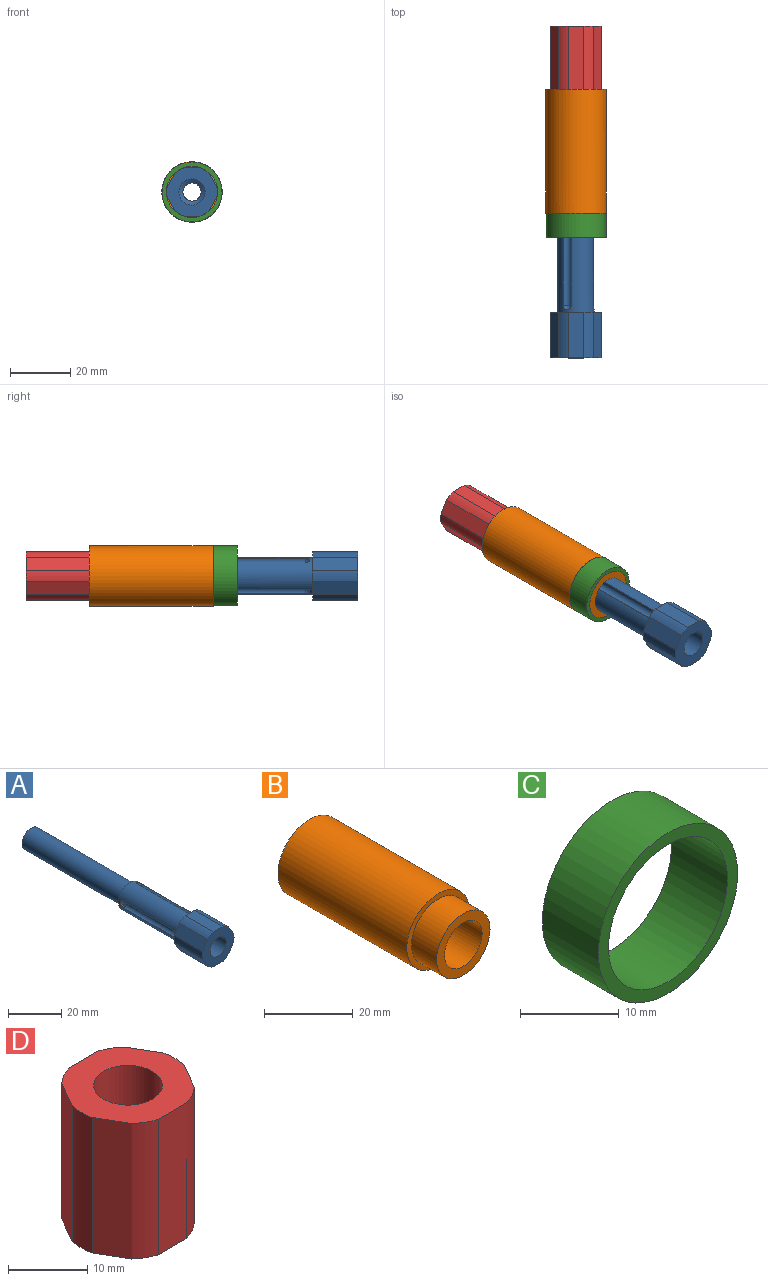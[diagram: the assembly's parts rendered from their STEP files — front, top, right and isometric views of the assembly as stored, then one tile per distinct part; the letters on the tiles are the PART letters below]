
ASSEMBLY  parts=4 mates=6
PART A: 30 faces, bbox 16.8x99.5x16 mm
  f0: sphere r=1.53mm, area 6.9mm2, adj f11,f29
  f1: sphere r=1.53mm, area 6.9mm2, adj f11,f29
  f2: sphere r=1.53mm, area 6.9mm2, adj f11,f28
  f3: sphere r=1.53mm, area 6.9mm2, adj f11,f28
  f4: sphere r=1.53mm, area 6.9mm2, adj f11,f27
  f5: sphere r=1.53mm, area 6.9mm2, adj f11,f27
  f6: cylinder r=8.4mm len=15mm, axis (0,1,0), area 53.9mm2, adj f12,f13,f16,f17
  f7: cylinder r=3mm len=84.69mm, axis (0,1,0), area 1596.3mm2, adj f8,f20
  f8: cone r=4.35mm half-angle=59deg, axis (0,-1,0), area 36.4mm2, adj f7,f9
  f9: cylinder r=4.35mm len=14mm, axis (0,1,0), area 382.6mm2, adj f8,f12
  f10: cylinder r=4.75mm len=52.5mm, axis (0,1,0), area 1566.9mm2, adj f20,f21
  f11: cylinder r=6mm len=32mm, axis (0,1,0), area 944.7mm2, adj f0,f1,f2,f3,f4,f5,f13,f21
  f12: plane 16.8x16mm, normal (0,-1,0), area 154mm2, adj f6,f9,f14,f15,f16,f17,f18,f19
  f13: plane 16.8x16mm, normal (0,1,0), area 100.3mm2, adj f6,f11,f14,f15,f16,f17,f18,f19
  f14: plane 15x4.44mm, normal (0.87,0,-0.5), area 76.8mm2, adj f12,f13,f23,f26
  f15: plane 15x5.12mm, normal (0,0,-1), area 76.8mm2, adj f12,f13,f25,f26
  f16: plane 15x4.44mm, normal (-0.87,0,-0.5), area 76.8mm2, adj f6,f12,f13,f25
  f17: plane 15x4.44mm, normal (-0.87,0,0.5), area 76.8mm2, adj f6,f12,f13,f24
  f18: plane 15x5.12mm, normal (0,0,1), area 76.8mm2, adj f12,f13,f22,f24
  f19: plane 15x4.44mm, normal (0.87,0,0.5), area 76.8mm2, adj f12,f13,f22,f23
  f20: plane 9.5x9.5mm, normal (0,1,0), area 42.6mm2, adj f7,f10
  f21: plane 12x12mm, normal (0,1,0), area 42.2mm2, adj f10,f11
  f22: cylinder r=8.4mm len=15mm, axis (0,1,0), area 53.9mm2, adj f12,f13,f18,f19
  f23: cylinder r=8.4mm len=15mm, axis (0,1,0), area 53.9mm2, adj f12,f13,f14,f19
  f24: cylinder r=8.4mm len=15mm, axis (0,1,0), area 53.9mm2, adj f12,f13,f17,f18
  f25: cylinder r=8.4mm len=15mm, axis (0,1,0), area 53.9mm2, adj f12,f13,f15,f16
  f26: cylinder r=8.4mm len=15mm, axis (0,1,0), area 53.9mm2, adj f12,f13,f14,f15
  f27: cylinder r=1.53mm len=27mm, axis (0,1,0), area 118.9mm2, adj f4,f5,f11
  f28: cylinder r=1.53mm len=27mm, axis (0,1,0), area 118.9mm2, adj f2,f3,f11
  f29: cylinder r=1.53mm len=27mm, axis (0,1,0), area 118.9mm2, adj f0,f1,f11
PART B: 8 faces, bbox 20x49x20 mm
  f0: cylinder r=8.5mm len=17mm, axis (0,1,0), area 427.3mm2, adj f4,f7
  f1: cylinder r=4.75mm len=9.5mm, axis (0,1,0), area 208.9mm2, adj f5,f6
  f2: cylinder r=6mm len=42mm, axis (0,1,0), area 1583.4mm2, adj f4,f6
  f3: cylinder r=10mm len=41mm, axis (0,1,0), area 2576.1mm2, adj f5,f7
  f4: plane 17x17mm, normal (0,-1,0), area 113.9mm2, adj f0,f2
  f5: plane 20x20mm, normal (0,1,0), area 243.3mm2, adj f1,f3
  f6: plane 12x12mm, normal (0,-1,0), area 42.2mm2, adj f1,f2
  f7: plane 20x20mm, normal (0,-1,0), area 87.2mm2, adj f0,f3
PART C: 4 faces, bbox 19.9x8x19.9 mm
  f0: cylinder r=9.95mm len=19.9mm, axis (0,-1,0), area 500.1mm2, adj f2,f3
  f1: cylinder r=8.5mm len=17mm, axis (0,-1,0), area 427.3mm2, adj f2,f3
  f2: plane 19.9x19.9mm, normal (0,1,0), area 84mm2, adj f0,f1
  f3: plane 19.9x19.9mm, normal (0,-1,0), area 84mm2, adj f0,f1
PART D: 19 faces, bbox 16.8x16x21 mm
  f0: cylinder r=4.35mm len=9mm, axis (0,0,-1), area 246mm2, adj f11,f18
  f1: cylinder r=4.35mm len=10.5mm, axis (0,0,-1), area 287mm2, adj f4,f17
  f2: cylinder r=8.4mm len=21mm, axis (0,0,1), area 75.4mm2, adj f4,f5,f10,f11
  f3: cylinder r=3mm len=6mm, axis (0,0,1), area 28.3mm2, adj f17,f18
  f4: plane 16.8x16mm, normal (0,0,1), area 154mm2, adj f1,f2,f5,f6,f7,f8,f9,f10
  f5: plane 21x4.44mm, normal (0.87,-0.5,0), area 107.6mm2, adj f2,f4,f11,f16
  f6: plane 21x5.12mm, normal (0,-1,0), area 107.6mm2, adj f4,f11,f15,f16
  f7: plane 21x4.44mm, normal (-0.87,-0.5,0), area 107.6mm2, adj f4,f11,f14,f15
  f8: plane 21x4.44mm, normal (-0.87,0.5,0), area 107.6mm2, adj f4,f11,f13,f14
  f9: plane 21x5.12mm, normal (0,1,0), area 107.6mm2, adj f4,f11,f12,f13
  f10: plane 21x4.44mm, normal (0.87,0.5,0), area 107.6mm2, adj f2,f4,f11,f12
  f11: plane 16.8x16mm, normal (0,0,-1), area 154mm2, adj f0,f2,f5,f6,f7,f8,f9,f10
  f12: cylinder r=8.4mm len=21mm, axis (0,0,1), area 75.4mm2, adj f4,f9,f10,f11
  f13: cylinder r=8.4mm len=21mm, axis (0,0,1), area 75.4mm2, adj f4,f8,f9,f11
  f14: cylinder r=8.4mm len=21mm, axis (0,0,1), area 75.4mm2, adj f4,f7,f8,f11
  f15: cylinder r=8.4mm len=21mm, axis (0,0,1), area 75.4mm2, adj f4,f6,f7,f11
  f16: cylinder r=8.4mm len=21mm, axis (0,0,1), area 75.4mm2, adj f4,f5,f6,f11
  f17: plane 8.7x8.7mm, normal (0,0,1), area 31.2mm2, adj f1,f3
  f18: plane 8.7x8.7mm, normal (0,0,-1), area 31.2mm2, adj f0,f3
PLACE A rot(axis=(0,1,0),180deg) t=(-5.1,92.86,70.84)mm
PLACE B t=(-5.1,82.36,70.84)mm
PLACE C rot(axis=(0,1,0),180deg) t=(-5.1,33.36,70.84)mm
PLACE D rot(axis=(1,0,0),90deg) t=(-5.1,82.36,70.84)mm
MATE cylindrical A.f6 <-> B.f1  axis (0,1,0) through (-5.1,66.61,70.84)mm
MATE planar D.f0 <-> A.f6  axis (0,-1,0) through (-5.1,92.86,70.84)mm
MATE planar B.f0 <-> D.f4  axis (0,1,0) through (-5.1,82.36,70.84)mm
MATE planar C.f0 <-> B.f1  axis (0,1,0) through (-5.1,41.36,70.84)mm
MATE cylindrical B.f0 <-> C.f0  axis (0,1,0) through (-5.1,41.36,70.84)mm
MATE cylindrical D.f0 <-> A.f6  axis (0,1,0) through (-5.1,82.36,70.84)mm
